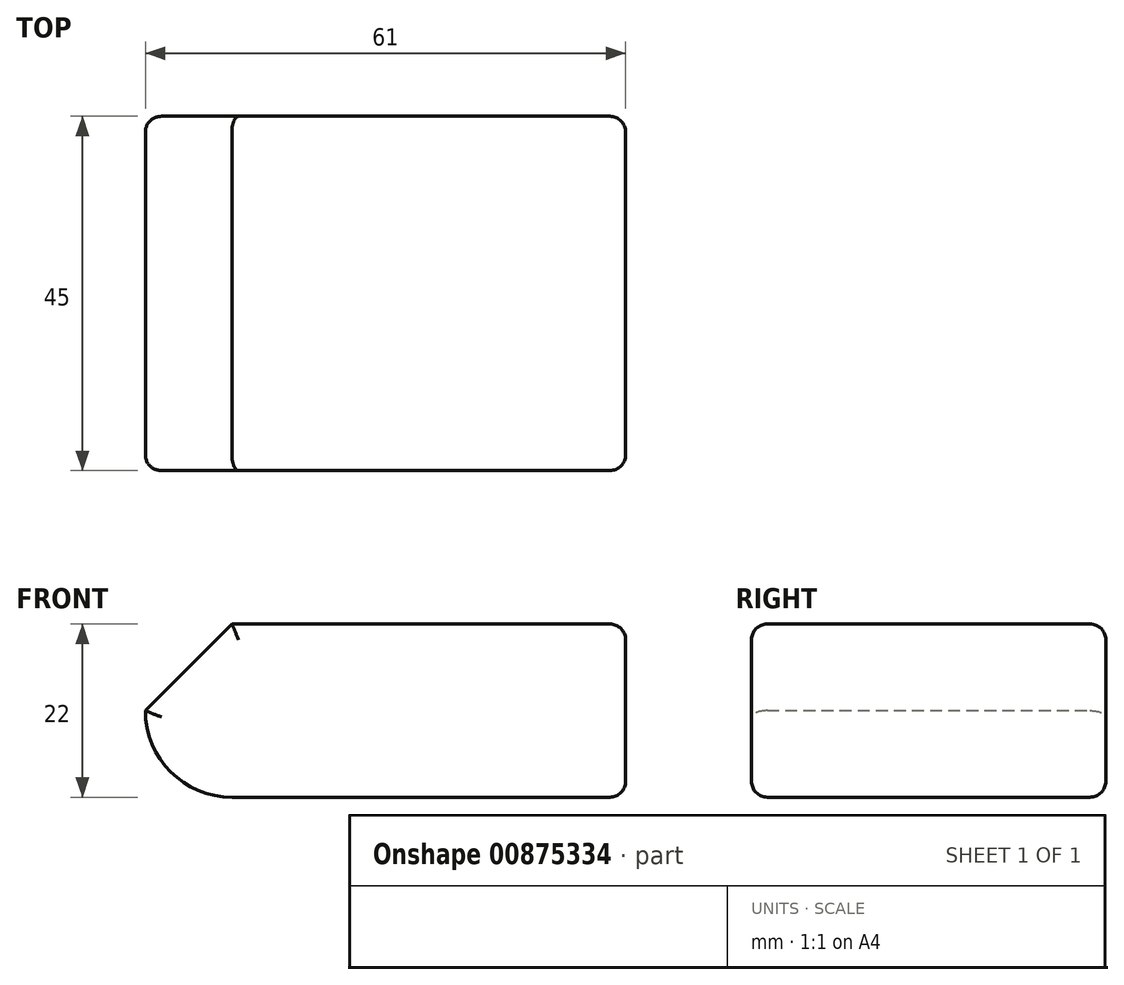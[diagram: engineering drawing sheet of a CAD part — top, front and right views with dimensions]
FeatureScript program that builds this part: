
annotation { "Feature Type Name" : "Feature", "Feature Type Description" : "" }
export const myFeature = defineFeature(function(context is Context, id is Id, definition is map)
    precondition{}
    {
        {
            var Q0;
            Q0=qCreatedBy(makeId("Front.planeOp"),FACE);
            var sketch = newSketch(context, id + "F0", { "sketchPlane" : qUnion([Q0])});
            skLineSegment(sketch, "E0.bottom", {"start": v(-25, 11) * mm, "end": v(25, 11) * mm});
            skLineSegment(sketch, "E0.top", {"start": v(-25, -11) * mm, "end": v(25, -11) * mm});
            skLineSegment(sketch, "E0.left", {"start": v(-25, 11) * mm, "end": v(-25, -11) * mm});
            skLineSegment(sketch, "E0.right", {"start": v(25, 11) * mm, "end": v(25, -11) * mm});
            skPoint(sketch, "E0.middle", {"position": v(0, 0) * mm});
            skCircle(sketch, "E1", {"center": v(-25, 0) * mm, "radius": 11 * mm});
            skLineSegment(sketch, "E2", {"start": v(-25, 11) * mm, "end": v(-36, 0) * mm});
            skSolve(sketch);
        }
        {
            var Q0;
            {var subQ0=sQuery(id+"F0.wireOp",EDGE,"E0.bottom");Q0=makeQuery(id+"F0.imprint","IMPRINT",FACE,{"disambiguationData":[TD([[makeQuery(id+"F0.imprint","IMPRINT",EDGE,{"derivedFrom":subQ0}),-1.0]])]});}
            var Q1;
            {var subQ0=sQuery(id+"F0.wireOp",EDGE,"E0.left");Q1=makeQuery(id+"F0.imprint","IMPRINT",FACE,{"disambiguationData":[TD([[makeQuery(id+"F0.imprint","IMPRINT",EDGE,{"derivedFrom":subQ0}),-1.0]])]});}
            var Q2;
            {var subQ0=sQuery(id+"F0.wireOp",EDGE,"E0.left");Q2=makeQuery(id+"F0.imprint","IMPRINT",FACE,{"disambiguationData":[TD([[makeQuery(id+"F0.imprint","IMPRINT",EDGE,{"derivedFrom":subQ0}),1.0]])]});}
            extrude(context, id + "F1", {"entities" : qUnion([Q0, Q1, Q2]), "depth" : 45 * mm, "offsetDistance" : 25.4 * mm});
        }
        {
            var Q0;
            Q0=makeQuery(id+"F1.opExtrude","CAP_FACE",FACE,{"disambiguationData":[OSD([sQuery(id+"F0.wireOp",EDGE,"E0.bottom"),sQuery(id+"F0.wireOp",EDGE,"E0.top"),sQuery(id+"F0.wireOp",EDGE,"E0.right"),sQuery(id+"F0.wireOp",EDGE,"E1"),sQuery(id+"F0.wireOp",EDGE,"E2")])],"isStart":false});
            var Q1;
            Q1=makeQuery(id+"F1.opExtrude","CAP_FACE",FACE,{"disambiguationData":[OSD([sQuery(id+"F0.wireOp",EDGE,"E0.bottom"),sQuery(id+"F0.wireOp",EDGE,"E0.top"),sQuery(id+"F0.wireOp",EDGE,"E0.right"),sQuery(id+"F0.wireOp",EDGE,"E1"),sQuery(id+"F0.wireOp",EDGE,"E2")])],"isStart":true});
            var Q2;
            Q2=makeQuery(id+"F1.opExtrude","SWEPT_FACE",FACE,{"disambiguationData":[OSD([sQuery(id+"F0.wireOp",EDGE,"E0.right")])]});
            fillet(context, id + "F2", {"entities" : qUnion([Q0, Q1, Q2]), "radius" : 2 * mm, "tangentPropagation" : true, "allowEdgeOverflow" : false});
        }
    });
